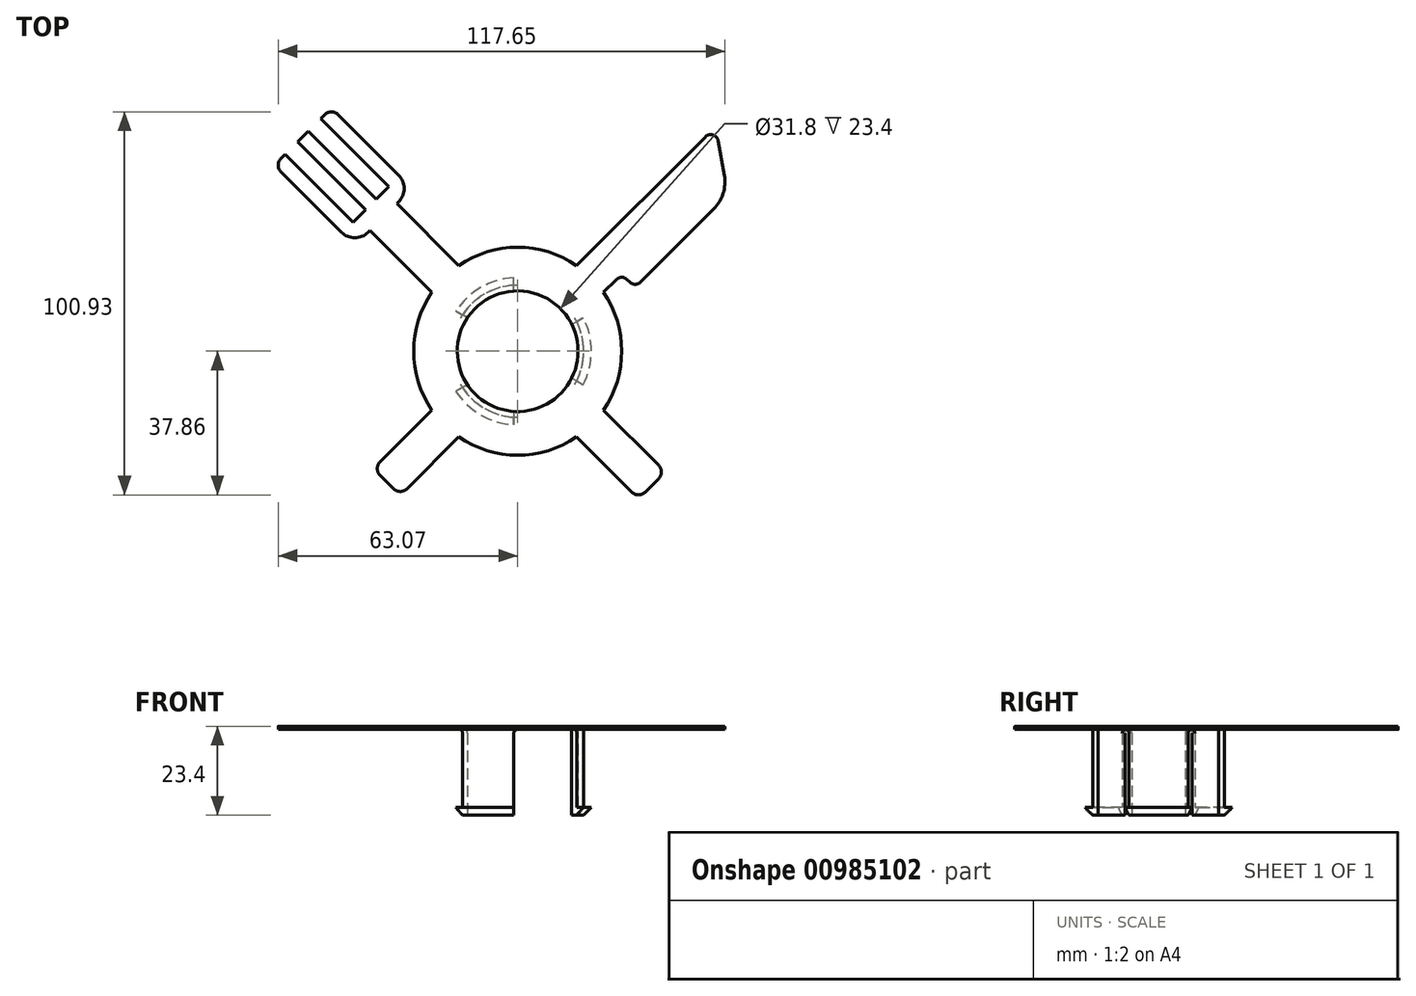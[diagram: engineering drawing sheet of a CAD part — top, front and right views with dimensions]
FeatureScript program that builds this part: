
annotation { "Feature Type Name" : "Feature", "Feature Type Description" : "" }
export const myFeature = defineFeature(function(context is Context, id is Id, definition is map)
    precondition{}
    {
        {
            var Q0;
            Q0=qCreatedBy(makeId("Top.planeOp"),FACE);
            var sketch = newSketch(context, id + "F0", { "sketchPlane" : qUnion([Q0])});
            skCircle(sketch, "E0", {"center": v(0, 0) * mm, "radius": 17.4 * mm});
            skCircle(sketch, "E1", {"center": v(0, 0) * mm, "radius": 15.9 * mm});
            skCircle(sketch, "E2", {"center": v(0, 0) * mm, "radius": 27.4 * mm});
            skLineSegment(sketch, "E3", {"start": v(0, 0) * mm, "end": v(0, 17.75) * mm, "construction": true});
            skText(sketch, "E4", { "text": "o", "fontName": "RobotoSlab-Bold.ttf"});
            skText(sketch, "E5", { "text": "u", "fontName": "RobotoSlab-Bold.ttf"});
            skText(sketch, "E6", { "text": "e", "fontName": "RobotoSlab-Bold.ttf"});
            skText(sketch, "E7", { "text": "i", "fontName": "RobotoSlab-Bold.ttf"});
            skText(sketch, "E8", { "text": "r", "fontName": "RobotoSlab-Bold.ttf"});
            skText(sketch, "E9", { "text": "c", "fontName": "RobotoSlab-Bold.ttf"});
            skText(sketch, "E10", { "text": "e", "fontName": "RobotoSlab-Bold.ttf"});
            skText(sketch, "E11", { "text": "o", "fontName": "RobotoSlab-Bold.ttf"});
            skText(sketch, "E12", { "text": "r", "fontName": "RobotoSlab-Bold.ttf"});
            skText(sketch, "E13", { "text": "n", "fontName": "RobotoSlab-Bold.ttf"});
            skLineSegment(sketch, "E14.2.0", {"start": v(0, 0) * mm, "end": v(-15.37, 8.88) * mm, "construction": true});
            skLineSegment(sketch, "E14.3.0", {"start": v(0, 0) * mm, "end": v(-17.75, 0) * mm, "construction": true});
            skLineSegment(sketch, "E14.4.0", {"start": v(0, 0) * mm, "end": v(-15.37, -8.88) * mm, "construction": true});
            skLineSegment(sketch, "E14.5.0", {"start": v(0, 0) * mm, "end": v(-8.88, -15.37) * mm, "construction": true});
            skLineSegment(sketch, "E14.6.0", {"start": v(0, 0) * mm, "end": v(0, -17.75) * mm, "construction": true});
            skLineSegment(sketch, "E14.7.0", {"start": v(0, 0) * mm, "end": v(8.87, -15.37) * mm, "construction": true});
            skLineSegment(sketch, "E14.8.0", {"start": v(0, 0) * mm, "end": v(15.37, -8.88) * mm, "construction": true});
            skLineSegment(sketch, "E14.9.0", {"start": v(0, 0) * mm, "end": v(17.75, 0) * mm, "construction": true});
            skLineSegment(sketch, "E14.10.0", {"start": v(0, 0) * mm, "end": v(15.37, 8.87) * mm, "construction": true});
            skLineSegment(sketch, "E14.11.0", {"start": v(0, 0) * mm, "end": v(8.88, 15.37) * mm, "construction": true});
            skText(sketch, "E15", { "text": "S", "fontName": "RobotoSlab-Bold.ttf"});
            skLineSegment(sketch, "E16", {"start": v(0, 0) * mm, "end": v(-8.88, 15.37) * mm, "construction": true});
            const initialGuessF0  = {"E4": [-0.00328, 0.01775, 1, 0, 0.008], "E5": [0.0057, 0.0172, 0.86603, -0.5, 0.008], "E6": [0.01692, -0.0062, -0.5, -0.86603, 0.008], "E7": [-0.0071, -0.0164, -0.86603, 0.5, 0.008], "E8": [-0.01407, -0.01114, -0.5, 0.86603, 0.008], "E9": [0.01775, 0.0031, 0, -1, 0.008], "E10": [0.01156, -0.01382, -0.86603, -0.5, 0.008], "E11": [-0.01775, -0.00328, 0, 1, 0.008], "E12": [0.01407, 0.01114, 0.5, -0.86603, 0.008], "E13": [-0.01726, 0.0056, 0.5, 0.86603, 0.008], "E15": [-0.01195, 0.0136, 0.86603, 0.5, 0.008]};
            skSetInitialGuess(sketch, initialGuessF0);
            skSolve(sketch);
        }
        {
            var Q0;
            Q0=makeQuery(id+"F0.imprint","IMPRINT",FACE,{"disambiguationData":[TD([[makeQuery(id+"F0.imprint","IMPRINT",EDGE,{"derivedFrom":sQuery(id+"F0.wireOp",EDGE,"E0")}),1.0]])]});
            var Q1;
            Q1=makeQuery(id+"F0.imprint","IMPRINT",FACE,{"disambiguationData":[TD([[makeQuery(id+"F0.imprint","IMPRINT",EDGE,{"derivedFrom":sQuery(id+"F0.wireOp",EDGE,"E4.sketch_text.stroke-0")}),-1.0]])]});
            var Q2;
            Q2=makeQuery(id+"F0.imprint","IMPRINT",FACE,{"disambiguationData":[TD([[makeQuery(id+"F0.imprint","IMPRINT",EDGE,{"derivedFrom":sQuery(id+"F0.wireOp",EDGE,"E7.sketch_text.stroke-0")}),-1.0]])]});
            var Q3;
            Q3=makeQuery(id+"F0.imprint","IMPRINT",FACE,{"disambiguationData":[TD([[makeQuery(id+"F0.imprint","IMPRINT",EDGE,{"derivedFrom":sQuery(id+"F0.wireOp",EDGE,"E11.sketch_text.stroke-10")}),1.0]])]});
            var Q4;
            Q4=makeQuery(id+"F0.imprint","IMPRINT",FACE,{"disambiguationData":[TD([[makeQuery(id+"F0.imprint","IMPRINT",EDGE,{"derivedFrom":sQuery(id+"F0.wireOp",EDGE,"E9.sketch_text.stroke-0")}),-1.0]])]});
            var Q5;
            Q5=makeQuery(id+"F0.imprint","IMPRINT",FACE,{"disambiguationData":[TD([[makeQuery(id+"F0.imprint","IMPRINT",EDGE,{"derivedFrom":sQuery(id+"F0.wireOp",EDGE,"E10.sketch_text.stroke-0")}),-1.0]])]});
            var Q6;
            Q6=makeQuery(id+"F0.imprint","IMPRINT",FACE,{"disambiguationData":[TD([[makeQuery(id+"F0.imprint","IMPRINT",EDGE,{"derivedFrom":sQuery(id+"F0.wireOp",EDGE,"E6.sketch_text.stroke-0")}),-1.0]])]});
            var Q7;
            Q7=makeQuery(id+"F0.imprint","IMPRINT",FACE,{"disambiguationData":[TD([[makeQuery(id+"F0.imprint","IMPRINT",EDGE,{"derivedFrom":sQuery(id+"F0.wireOp",EDGE,"E12.sketch_text.stroke-0")}),-1.0]])]});
            var Q8;
            Q8=makeQuery(id+"F0.imprint","IMPRINT",FACE,{"disambiguationData":[TD([[makeQuery(id+"F0.imprint","IMPRINT",EDGE,{"derivedFrom":sQuery(id+"F0.wireOp",EDGE,"E5.sketch_text.stroke-0")}),-1.0]])]});
            var Q9;
            Q9=makeQuery(id+"F0.imprint","IMPRINT",FACE,{"disambiguationData":[TD([[makeQuery(id+"F0.imprint","IMPRINT",EDGE,{"derivedFrom":sQuery(id+"F0.wireOp",EDGE,"E0")}),-1.0]])]});
            var Q10;
            Q10=makeQuery(id+"F0.imprint","IMPRINT",FACE,{"disambiguationData":[TD([[makeQuery(id+"F0.imprint","IMPRINT",EDGE,{"derivedFrom":sQuery(id+"F0.wireOp",EDGE,"E5.sketch_text.stroke-10")}),1.0]])]});
            var Q11;
            Q11=makeQuery(id+"F0.imprint","IMPRINT",FACE,{"disambiguationData":[TD([[makeQuery(id+"F0.imprint","IMPRINT",EDGE,{"derivedFrom":sQuery(id+"F0.wireOp",EDGE,"E13.sketch_text.stroke-0")}),-1.0]])]});
            var Q12;
            Q12=makeQuery(id+"F0.imprint","IMPRINT",FACE,{"disambiguationData":[TD([[makeQuery(id+"F0.imprint","IMPRINT",EDGE,{"derivedFrom":sQuery(id+"F0.wireOp",EDGE,"E8.sketch_text.stroke-0")}),-1.0]])]});
            var Q13;
            Q13=makeQuery(id+"F0.imprint","IMPRINT",FACE,{"disambiguationData":[TD([[makeQuery(id+"F0.imprint","IMPRINT",EDGE,{"derivedFrom":sQuery(id+"F0.wireOp",EDGE,"E11.sketch_text.stroke-0")}),-1.0]])]});
            var Q14;
            Q14=makeQuery(id+"F0.imprint","IMPRINT",FACE,{"disambiguationData":[TD([[makeQuery(id+"F0.imprint","IMPRINT",EDGE,{"derivedFrom":sQuery(id+"F0.wireOp",EDGE,"E7.sketch_text.stroke-10")}),-1.0]])]});
            var Q15;
            Q15=makeQuery(id+"F0.imprint","IMPRINT",FACE,{"disambiguationData":[TD([[makeQuery(id+"F0.imprint","IMPRINT",EDGE,{"derivedFrom":sQuery(id+"F0.wireOp",EDGE,"E10.sketch_text.stroke-17")}),1.0]])]});
            var Q16;
            Q16=makeQuery(id+"F0.imprint","IMPRINT",FACE,{"disambiguationData":[TD([[makeQuery(id+"F0.imprint","IMPRINT",EDGE,{"derivedFrom":sQuery(id+"F0.wireOp",EDGE,"E15.sketch_text.stroke-0")}),-1.0]])]});
            var Q17;
            Q17=makeQuery(id+"F0.imprint","IMPRINT",FACE,{"disambiguationData":[TD([[makeQuery(id+"F0.imprint","IMPRINT",EDGE,{"derivedFrom":sQuery(id+"F0.wireOp",EDGE,"E4.sketch_text.stroke-10")}),1.0]])]});
            var Q18;
            Q18=makeQuery(id+"F0.imprint","IMPRINT",FACE,{"disambiguationData":[TD([[makeQuery(id+"F0.imprint","IMPRINT",EDGE,{"derivedFrom":sQuery(id+"F0.wireOp",EDGE,"E6.sketch_text.stroke-17")}),1.0]])]});
            extrude(context, id + "F1", {"entities" : qUnion([Q0, Q1, Q2, Q3, Q4, Q5, Q6, Q7, Q8, Q9, Q10, Q11, Q12, Q13, Q14, Q15, Q16, Q17, Q18]), "depth" : 0.8 * mm, "offsetDistance" : 25 * mm});
        }
        {
            var Q0;
            Q0=makeQuery(id+"F0.imprint","IMPRINT",FACE,{"disambiguationData":[TD([[makeQuery(id+"F0.imprint","IMPRINT",EDGE,{"derivedFrom":sQuery(id+"F0.wireOp",EDGE,"E0")}),1.0]])]});
            extrude(context, id + "F2", {"entities" : qUnion([Q0]), "operationType" : NewBodyOperationType.ADD, "oppositeDirection" : true, "depth" : 22.6 * mm, "offsetDistance" : 25 * mm});
        }
        {
            var Q0;
            Q0=makeQuery(id+"F2.opExtrude","CAP_FACE",FACE,{"disambiguationData":[OSD([sQuery(id+"F0.wireOp",EDGE,"E0"),sQuery(id+"F0.wireOp",EDGE,"E1")])],"isStart":false});
            var sketch = newSketch(context, id + "F3", { "sketchPlane" : qUnion([Q0])});
            skLineSegment(sketch, "E17.bottom", {"start": v(1, 0) * mm, "end": v(-1, 0) * mm});
            skLineSegment(sketch, "E17.top", {"start": v(1, -20) * mm, "end": v(-1, -20) * mm});
            skLineSegment(sketch, "E17.left", {"start": v(1, 0) * mm, "end": v(1, -20) * mm});
            skLineSegment(sketch, "E17.right", {"start": v(-1, 0) * mm, "end": v(-1, -20) * mm});
            skLineSegment(sketch, "E18.1.0", {"start": v(0.5, 0.87) * mm, "end": v(-0.5, -0.87) * mm});
            skLineSegment(sketch, "E18.1.1", {"start": v(17.82, -9.13) * mm, "end": v(16.82, -10.87) * mm});
            skLineSegment(sketch, "E18.1.2", {"start": v(-0.5, -0.87) * mm, "end": v(16.82, -10.87) * mm});
            skLineSegment(sketch, "E18.1.3", {"start": v(0.5, 0.87) * mm, "end": v(17.82, -9.13) * mm});
            skLineSegment(sketch, "E18.2.0", {"start": v(-0.5, 0.87) * mm, "end": v(0.5, -0.87) * mm});
            skLineSegment(sketch, "E18.2.1", {"start": v(16.82, 10.87) * mm, "end": v(17.82, 9.13) * mm});
            skLineSegment(sketch, "E18.2.2", {"start": v(0.5, -0.87) * mm, "end": v(17.82, 9.13) * mm});
            skLineSegment(sketch, "E18.2.3", {"start": v(-0.5, 0.87) * mm, "end": v(16.82, 10.87) * mm});
            skLineSegment(sketch, "E18.3.0", {"start": v(-1, 0) * mm, "end": v(1, 0) * mm});
            skLineSegment(sketch, "E18.3.1", {"start": v(-1, 20) * mm, "end": v(1, 20) * mm});
            skLineSegment(sketch, "E18.3.2", {"start": v(1, 0) * mm, "end": v(1, 20) * mm});
            skLineSegment(sketch, "E18.3.3", {"start": v(-1, 0) * mm, "end": v(-1, 20) * mm});
            skLineSegment(sketch, "E18.4.0", {"start": v(-0.5, -0.87) * mm, "end": v(0.5, 0.87) * mm});
            skLineSegment(sketch, "E18.4.1", {"start": v(-17.82, 9.13) * mm, "end": v(-16.82, 10.87) * mm});
            skLineSegment(sketch, "E18.4.2", {"start": v(0.5, 0.87) * mm, "end": v(-16.82, 10.87) * mm});
            skLineSegment(sketch, "E18.4.3", {"start": v(-0.5, -0.87) * mm, "end": v(-17.82, 9.13) * mm});
            skLineSegment(sketch, "E18.5.0", {"start": v(0.5, -0.87) * mm, "end": v(-0.5, 0.87) * mm});
            skLineSegment(sketch, "E18.5.1", {"start": v(-16.82, -10.87) * mm, "end": v(-17.82, -9.13) * mm});
            skLineSegment(sketch, "E18.5.2", {"start": v(-0.5, 0.87) * mm, "end": v(-17.82, -9.13) * mm});
            skLineSegment(sketch, "E18.5.3", {"start": v(0.5, -0.87) * mm, "end": v(-16.82, -10.87) * mm});
            skPoint(sketch, "E18.center", {"position": v(0, 0) * mm});
            skCircle(sketch, "E19", {"center": v(0, 0) * mm, "radius": 19.4 * mm});
            skSolve(sketch);
        }
        {
            var Q0;
            {var subQ0=sQuery(id+"F3.wireOp",EDGE,"E18.1.2");var subQ1=makeQuery(id+"F2.opExtrude","CAP_EDGE",EDGE,{"disambiguationData":[OSD([sQuery(id+"F0.wireOp",EDGE,"E1")])],"isStart":false});var subQ2=makeQuery(id+"F3.imprint","INTERSECT",VERTEX,{"derivedFrom":[subQ1,subQ0]});Q0=makeQuery(id+"F3.imprint","IMPRINT",FACE,{"disambiguationData":[TD([[makeQuery(id+"F3.imprint","IMPRINT",EDGE,{"disambiguationData":[TD([[subQ2,-1.0]])],"derivedFrom":subQ0}),1.0]])]});}
            var Q1;
            {var subQ0=sQuery(id+"F3.wireOp",EDGE,"E17.left");var subQ1=makeQuery(id+"F2.opExtrude","CAP_EDGE",EDGE,{"disambiguationData":[OSD([sQuery(id+"F0.wireOp",EDGE,"E1")])],"isStart":false});var subQ2=makeQuery(id+"F3.imprint","INTERSECT",VERTEX,{"derivedFrom":[subQ1,subQ0]});Q1=makeQuery(id+"F3.imprint","IMPRINT",FACE,{"disambiguationData":[TD([[makeQuery(id+"F3.imprint","IMPRINT",EDGE,{"disambiguationData":[TD([[subQ2,-1.0]])],"derivedFrom":subQ0}),-1.0]])]});}
            var Q2;
            {var subQ0=sQuery(id+"F3.wireOp",EDGE,"E18.5.2");var subQ1=makeQuery(id+"F2.opExtrude","CAP_EDGE",EDGE,{"disambiguationData":[OSD([sQuery(id+"F0.wireOp",EDGE,"E1")])],"isStart":false});var subQ2=makeQuery(id+"F3.imprint","INTERSECT",VERTEX,{"derivedFrom":[subQ1,subQ0]});Q2=makeQuery(id+"F3.imprint","IMPRINT",FACE,{"disambiguationData":[TD([[makeQuery(id+"F3.imprint","IMPRINT",EDGE,{"disambiguationData":[TD([[subQ2,-1.0]])],"derivedFrom":subQ0}),1.0]])]});}
            var Q3;
            {var subQ0=sQuery(id+"F3.wireOp",EDGE,"E18.4.2");var subQ1=makeQuery(id+"F2.opExtrude","CAP_EDGE",EDGE,{"disambiguationData":[OSD([sQuery(id+"F0.wireOp",EDGE,"E1")])],"isStart":false});var subQ2=makeQuery(id+"F3.imprint","INTERSECT",VERTEX,{"derivedFrom":[subQ1,subQ0]});Q3=makeQuery(id+"F3.imprint","IMPRINT",FACE,{"disambiguationData":[TD([[makeQuery(id+"F3.imprint","IMPRINT",EDGE,{"disambiguationData":[TD([[subQ2,-1.0]])],"derivedFrom":subQ0}),1.0]])]});}
            var Q4;
            {var subQ0=sQuery(id+"F3.wireOp",EDGE,"E18.3.2");var subQ1=makeQuery(id+"F2.opExtrude","CAP_EDGE",EDGE,{"disambiguationData":[OSD([sQuery(id+"F0.wireOp",EDGE,"E1")])],"isStart":false});var subQ2=makeQuery(id+"F3.imprint","INTERSECT",VERTEX,{"derivedFrom":[subQ1,subQ0]});Q4=makeQuery(id+"F3.imprint","IMPRINT",FACE,{"disambiguationData":[TD([[makeQuery(id+"F3.imprint","IMPRINT",EDGE,{"disambiguationData":[TD([[subQ2,-1.0]])],"derivedFrom":subQ0}),1.0]])]});}
            var Q5;
            {var subQ0=sQuery(id+"F3.wireOp",EDGE,"E18.2.2");var subQ1=makeQuery(id+"F2.opExtrude","CAP_EDGE",EDGE,{"disambiguationData":[OSD([sQuery(id+"F0.wireOp",EDGE,"E1")])],"isStart":false});var subQ2=makeQuery(id+"F3.imprint","INTERSECT",VERTEX,{"derivedFrom":[subQ1,subQ0]});Q5=makeQuery(id+"F3.imprint","IMPRINT",FACE,{"disambiguationData":[TD([[makeQuery(id+"F3.imprint","IMPRINT",EDGE,{"disambiguationData":[TD([[subQ2,-1.0]])],"derivedFrom":subQ0}),1.0]])]});}
            var Q6;
            {var subQ0=sQuery(id+"F3.wireOp",EDGE,"E17.left");var subQ1=makeQuery(id+"F2.opExtrude","CAP_EDGE",EDGE,{"disambiguationData":[OSD([sQuery(id+"F0.wireOp",EDGE,"E1")])],"isStart":false});var subQ2=makeQuery(id+"F3.imprint","INTERSECT",VERTEX,{"derivedFrom":[subQ1,subQ0]});Q6=makeQuery(id+"F3.imprint","IMPRINT",FACE,{"disambiguationData":[TD([[makeQuery(id+"F3.imprint","IMPRINT",EDGE,{"disambiguationData":[TD([[subQ2,-1.0]])],"derivedFrom":subQ0}),1.0]])]});}
            var Q7;
            {var subQ0=sQuery(id+"F3.wireOp",EDGE,"E18.4.3");var subQ1=makeQuery(id+"F2.opExtrude","CAP_EDGE",EDGE,{"disambiguationData":[OSD([sQuery(id+"F0.wireOp",EDGE,"E1")])],"isStart":false});var subQ2=makeQuery(id+"F3.imprint","INTERSECT",VERTEX,{"derivedFrom":[subQ1,subQ0]});Q7=makeQuery(id+"F3.imprint","IMPRINT",FACE,{"disambiguationData":[TD([[makeQuery(id+"F3.imprint","IMPRINT",EDGE,{"disambiguationData":[TD([[subQ2,-1.0]])],"derivedFrom":subQ0}),1.0]])]});}
            var Q8;
            {var subQ0=sQuery(id+"F3.wireOp",EDGE,"E18.2.3");var subQ1=makeQuery(id+"F2.opExtrude","CAP_EDGE",EDGE,{"disambiguationData":[OSD([sQuery(id+"F0.wireOp",EDGE,"E1")])],"isStart":false});var subQ2=makeQuery(id+"F3.imprint","INTERSECT",VERTEX,{"derivedFrom":[subQ1,subQ0]});Q8=makeQuery(id+"F3.imprint","IMPRINT",FACE,{"disambiguationData":[TD([[makeQuery(id+"F3.imprint","IMPRINT",EDGE,{"disambiguationData":[TD([[subQ2,-1.0]])],"derivedFrom":subQ0}),1.0]])]});}
            var Q9;
            Q9=makeQuery(id+"F1.opExtrude","CAP_FACE",FACE,{"disambiguationData":[OSD([sQuery(id+"F0.wireOp",EDGE,"E1"),sQuery(id+"F0.wireOp",EDGE,"E2")])],"isStart":true});
            extrude(context, id + "F4", {"entities" : qUnion([Q0, Q1, Q2, Q3, Q4, Q5, Q6, Q7, Q8]), "operationType" : NewBodyOperationType.REMOVE, "endBound" : BoundingType.UP_TO_SURFACE, "oppositeDirection" : true, "depth" : 25 * mm, "endBoundEntityFace" : qUnion([Q9]), "offsetDistance" : 25 * mm});
        }
        {
            var Q0;
            {var subQ0=sQuery(id+"F3.wireOp",EDGE,"E19");var subQ1=sQuery(id+"F3.wireOp",EDGE,"E18.1.3");var subQ2=makeQuery(id+"F3.imprint","INTERSECT",VERTEX,{"derivedFrom":[subQ1,subQ0]});Q0=makeQuery(id+"F3.imprint","IMPRINT",FACE,{"disambiguationData":[TD([[makeQuery(id+"F3.imprint","IMPRINT",EDGE,{"disambiguationData":[TD([[subQ2,1.0]])],"derivedFrom":subQ1}),1.0]])]});}
            var Q1;
            {var subQ0=sQuery(id+"F3.wireOp",EDGE,"E19");var subQ1=sQuery(id+"F3.wireOp",EDGE,"E17.right");var subQ2=makeQuery(id+"F3.imprint","INTERSECT",VERTEX,{"derivedFrom":[subQ1,subQ0]});Q1=makeQuery(id+"F3.imprint","IMPRINT",FACE,{"disambiguationData":[TD([[makeQuery(id+"F3.imprint","IMPRINT",EDGE,{"disambiguationData":[TD([[subQ2,1.0]])],"derivedFrom":subQ1}),-1.0]])]});}
            var Q2;
            {var subQ0=sQuery(id+"F3.wireOp",EDGE,"E19");var subQ1=sQuery(id+"F3.wireOp",EDGE,"E18.3.3");var subQ2=makeQuery(id+"F3.imprint","INTERSECT",VERTEX,{"derivedFrom":[subQ1,subQ0]});Q2=makeQuery(id+"F3.imprint","IMPRINT",FACE,{"disambiguationData":[TD([[makeQuery(id+"F3.imprint","IMPRINT",EDGE,{"disambiguationData":[TD([[subQ2,1.0]])],"derivedFrom":subQ1}),1.0]])]});}
            extrude(context, id + "F5", {"entities" : qUnion([Q0, Q1, Q2]), "operationType" : NewBodyOperationType.ADD, "oppositeDirection" : true, "depth" : 2 * mm, "offsetDistance" : 25 * mm});
        }
        {
            var Q0;
            {var subQ0=sQuery(id+"F3.wireOp",EDGE,"E19");Q0=makeQuery(id+"F5.opExtrude","CAP_EDGE",EDGE,{"disambiguationData":[OSD([subQ0]),TDD([makeQuery(id+"F3.imprint","IMPRINT",EDGE,{"disambiguationData":[TD([[makeQuery(id+"F3.imprint","INTERSECT",VERTEX,{"derivedFrom":[sQuery(id+"F3.wireOp",EDGE,"E18.1.3"),subQ0]}),-1.0]])],"derivedFrom":subQ0})])],"isStart":true});}
            var Q1;
            {var subQ0=sQuery(id+"F3.wireOp",EDGE,"E19");Q1=makeQuery(id+"F5.opExtrude","CAP_EDGE",EDGE,{"disambiguationData":[OSD([subQ0]),TDD([makeQuery(id+"F3.imprint","IMPRINT",EDGE,{"disambiguationData":[TD([[makeQuery(id+"F3.imprint","INTERSECT",VERTEX,{"derivedFrom":[sQuery(id+"F3.wireOp",EDGE,"E18.2.3"),subQ0]}),-1.0]])],"derivedFrom":subQ0})])],"isStart":true});}
            var Q2;
            {var subQ0=sQuery(id+"F3.wireOp",EDGE,"E19");Q2=makeQuery(id+"F5.opExtrude","CAP_EDGE",EDGE,{"disambiguationData":[OSD([subQ0]),TDD([makeQuery(id+"F3.imprint","IMPRINT",EDGE,{"disambiguationData":[TD([[makeQuery(id+"F3.imprint","INTERSECT",VERTEX,{"derivedFrom":[sQuery(id+"F3.wireOp",EDGE,"E18.3.3"),subQ0]}),-1.0]])],"derivedFrom":subQ0})])],"isStart":true});}
            var Q3;
            {var subQ0=sQuery(id+"F3.wireOp",EDGE,"E19");Q3=makeQuery(id+"F5.opExtrude","CAP_EDGE",EDGE,{"disambiguationData":[OSD([subQ0]),TDD([makeQuery(id+"F3.imprint","IMPRINT",EDGE,{"disambiguationData":[TD([[makeQuery(id+"F3.imprint","INTERSECT",VERTEX,{"derivedFrom":[sQuery(id+"F3.wireOp",EDGE,"E17.right"),subQ0]}),1.0]])],"derivedFrom":subQ0})])],"isStart":true});}
            var Q4;
            {var subQ0=sQuery(id+"F3.wireOp",EDGE,"E19");Q4=makeQuery(id+"F5.opExtrude","CAP_EDGE",EDGE,{"disambiguationData":[OSD([subQ0]),TDD([makeQuery(id+"F3.imprint","IMPRINT",EDGE,{"disambiguationData":[TD([[makeQuery(id+"F3.imprint","INTERSECT",VERTEX,{"derivedFrom":[sQuery(id+"F3.wireOp",EDGE,"E17.left"),subQ0]}),-1.0]])],"derivedFrom":subQ0})])],"isStart":true});}
            var Q5;
            {var subQ0=sQuery(id+"F3.wireOp",EDGE,"E19");Q5=makeQuery(id+"F5.opExtrude","CAP_EDGE",EDGE,{"disambiguationData":[OSD([subQ0]),TDD([makeQuery(id+"F3.imprint","IMPRINT",EDGE,{"disambiguationData":[TD([[makeQuery(id+"F3.imprint","INTERSECT",VERTEX,{"derivedFrom":[sQuery(id+"F3.wireOp",EDGE,"E18.4.3"),subQ0]}),-1.0]])],"derivedFrom":subQ0})])],"isStart":true});}
            chamfer(context, id + "F6", {"entities" : qUnion([Q0, Q1, Q2, Q3, Q4, Q5]), "width" : 2 * mm, "tangentPropagation" : true});
        }
        {
            var Q0;
            {var subQ0=sQuery(id+"F3.wireOp",EDGE,"E17.right");var subQ2=sQuery(id+"F0.wireOp",EDGE,"E0");Q0=makeQuery(id+"F4.boolean.opBoolean","SPLIT",EDGE,{"disambiguationData":[TD([makeQuery(id+"F4.opExtrude","SWEPT_FACE",FACE,{"disambiguationData":[OSD([subQ0])]})])],"derivedFrom":makeQuery(id+"F2.opExtrude","CAP_EDGE",EDGE,{"disambiguationData":[OSD([subQ2])],"isStart":true})});}
            var Q1;
            {var subQ1=sQuery(id+"F0.wireOp",EDGE,"E0");var subQ2=sQuery(id+"F3.wireOp",EDGE,"E18.3.3");Q1=makeQuery(id+"F4.boolean.opBoolean","SPLIT",EDGE,{"disambiguationData":[TD([makeQuery(id+"F4.opExtrude","SWEPT_FACE",FACE,{"disambiguationData":[OSD([subQ2])]})])],"derivedFrom":makeQuery(id+"F2.opExtrude","CAP_EDGE",EDGE,{"disambiguationData":[OSD([subQ1])],"isStart":true})});}
            var Q2;
            {var subQ0=sQuery(id+"F3.wireOp",EDGE,"E18.1.3");var subQ2=sQuery(id+"F0.wireOp",EDGE,"E0");Q2=makeQuery(id+"F4.boolean.opBoolean","SPLIT",EDGE,{"disambiguationData":[TD([makeQuery(id+"F4.opExtrude","SWEPT_FACE",FACE,{"disambiguationData":[OSD([subQ0])]})])],"derivedFrom":makeQuery(id+"F2.opExtrude","CAP_EDGE",EDGE,{"disambiguationData":[OSD([subQ2])],"isStart":true})});}
            var Q3;
            Q3=makeQuery(id+"F4.boolean.opBoolean","COPY",EDGE,{"derivedFrom":makeQuery(id+"F4.opExtrude","CAP_EDGE",EDGE,{"disambiguationData":[OSD([sQuery(id+"F3.wireOp",EDGE,"E18.2.2")])],"isStart":false})});
            var Q4;
            Q4=makeQuery(id+"F4.boolean.opBoolean","COPY",EDGE,{"derivedFrom":makeQuery(id+"F4.opExtrude","CAP_EDGE",EDGE,{"disambiguationData":[OSD([sQuery(id+"F3.wireOp",EDGE,"E18.3.3")])],"isStart":false})});
            var Q5;
            Q5=makeQuery(id+"F4.boolean.opBoolean","COPY",EDGE,{"derivedFrom":makeQuery(id+"F4.opExtrude","CAP_EDGE",EDGE,{"disambiguationData":[OSD([sQuery(id+"F3.wireOp",EDGE,"E18.1.3")])],"isStart":false})});
            var Q6;
            Q6=makeQuery(id+"F4.boolean.opBoolean","COPY",EDGE,{"derivedFrom":makeQuery(id+"F4.opExtrude","CAP_EDGE",EDGE,{"disambiguationData":[OSD([sQuery(id+"F3.wireOp",EDGE,"E17.right")])],"isStart":false})});
            var Q7;
            Q7=makeQuery(id+"F4.boolean.opBoolean","COPY",EDGE,{"derivedFrom":makeQuery(id+"F4.opExtrude","CAP_EDGE",EDGE,{"disambiguationData":[OSD([sQuery(id+"F3.wireOp",EDGE,"E18.5.3")])],"isStart":false})});
            var Q8;
            Q8=makeQuery(id+"F4.boolean.opBoolean","COPY",EDGE,{"derivedFrom":makeQuery(id+"F4.opExtrude","CAP_EDGE",EDGE,{"disambiguationData":[OSD([sQuery(id+"F3.wireOp",EDGE,"E18.4.2")])],"isStart":false})});
            fillet(context, id + "F7", {"entities" : qUnion([Q0, Q1, Q2, Q3, Q4, Q5, Q6, Q7, Q8]), "radius" : 1 * mm, "tangentPropagation" : true, "allowEdgeOverflow" : false});
        }
        {
            var Q0;
            Q0=makeQuery(id+"F1.opExtrude","CAP_FACE",FACE,{"disambiguationData":[OSD([sQuery(id+"F0.wireOp",EDGE,"E1"),sQuery(id+"F0.wireOp",EDGE,"E2")])],"isStart":false});
            var sketch = newSketch(context, id + "F8", { "sketchPlane" : qUnion([Q0])});
            skLineSegment(sketch, "E20.bottom", {"start": v(-38.9, 31.82) * mm, "end": v(30.05, -37.12) * mm});
            skLineSegment(sketch, "E20.top", {"start": v(-31.82, 38.9) * mm, "end": v(37.12, -30.05) * mm});
            skLineSegment(sketch, "E20.left", {"start": v(-38.9, 31.82) * mm, "end": v(-31.82, 38.9) * mm});
            skLineSegment(sketch, "E20.right", {"start": v(33.59, -37.12) * mm, "end": v(37.12, -33.59) * mm});
            skPoint(sketch, "E20.middle", {"position": v(0, 0) * mm});
            skLineSegment(sketch, "E21", {"start": v(35.36, -35.36) * mm, "end": v(0, 0) * mm, "construction": true});
            skLineSegment(sketch, "E22", {"start": v(0, 0) * mm, "end": v(0, -3.91) * mm});
            skLineSegment(sketch, "E23", {"start": v(-35.36, 35.36) * mm, "end": v(-56.57, 56.57) * mm});
            skLineSegment(sketch, "E24", {"start": v(-56.57, 56.57) * mm, "end": v(-55.15, 57.98) * mm});
            skLineSegment(sketch, "E25", {"start": v(-55.15, 57.98) * mm, "end": v(-37.23, 40.06) * mm});
            skLineSegment(sketch, "E26", {"start": v(-37.23, 40.06) * mm, "end": v(-33.94, 43.35) * mm});
            skLineSegment(sketch, "E27", {"start": v(-33.94, 43.35) * mm, "end": v(-51.86, 61.28) * mm});
            skLineSegment(sketch, "E28", {"start": v(-51.86, 61.28) * mm, "end": v(-50.8, 62.34) * mm});
            skLineSegment(sketch, "E29", {"start": v(-47.26, 62.34) * mm, "end": v(-31.35, 46.43) * mm});
            skLineSegment(sketch, "E30", {"start": v(-31.35, 39.36) * mm, "end": v(-31.82, 38.9) * mm});
            skLineSegment(sketch, "E31.MirrorCS", {"start": v(-62.34, 47.26) * mm, "end": v(-46.43, 31.35) * mm});
            skLineSegment(sketch, "E32.MirrorCS", {"start": v(-56.57, 56.57) * mm, "end": v(-57.98, 55.15) * mm});
            skLineSegment(sketch, "E33.MirrorCS", {"start": v(-39.36, 31.35) * mm, "end": v(-38.9, 31.82) * mm});
            skLineSegment(sketch, "E34.MirrorCS", {"start": v(-57.98, 55.15) * mm, "end": v(-40.06, 37.23) * mm});
            skLineSegment(sketch, "E35.MirrorCS", {"start": v(-61.28, 51.86) * mm, "end": v(-62.34, 50.8) * mm});
            skLineSegment(sketch, "E36.MirrorCS", {"start": v(-43.35, 33.94) * mm, "end": v(-61.28, 51.86) * mm});
            skLineSegment(sketch, "E37.MirrorCS", {"start": v(-40.06, 37.23) * mm, "end": v(-43.35, 33.94) * mm});
            skPoint(sketch, "E38.visualSharp", {"position": v(-42.9, 27.82) * mm});
            skArc(sketch, "E38.filletArc", {"start": v(-46.43, 31.35) * mm, "mid": v(-42.9, 29.89) * mm, "end": v(-39.36, 31.35) * mm});
            skPoint(sketch, "E39.visualSharp", {"position": v(-27.82, 42.9) * mm});
            skArc(sketch, "E39.filletArc", {"start": v(-31.35, 39.36) * mm, "mid": v(-29.89, 42.9) * mm, "end": v(-31.35, 46.43) * mm});
            skPoint(sketch, "E40.visualSharp", {"position": v(31.82, -38.9) * mm});
            skArc(sketch, "E40.filletArc", {"start": v(30.05, -37.12) * mm, "mid": v(31.82, -37.86) * mm, "end": v(33.59, -37.12) * mm});
            skPoint(sketch, "E41.visualSharp", {"position": v(38.9, -31.82) * mm});
            skArc(sketch, "E41.filletArc", {"start": v(37.12, -33.59) * mm, "mid": v(37.86, -31.82) * mm, "end": v(37.12, -30.05) * mm});
            skPoint(sketch, "E42.visualSharp", {"position": v(-64.1, 49.03) * mm});
            skArc(sketch, "E42.filletArc", {"start": v(-62.34, 50.8) * mm, "mid": v(-63.07, 49.03) * mm, "end": v(-62.34, 47.26) * mm});
            skPoint(sketch, "E43.visualSharp", {"position": v(-49.03, 64.1) * mm});
            skArc(sketch, "E43.filletArc", {"start": v(-47.26, 62.34) * mm, "mid": v(-49.03, 63.07) * mm, "end": v(-50.8, 62.34) * mm});
            skLineSegment(sketch, "E44.bottom", {"start": v(-29.17, -36.24) * mm, "end": v(25.99, 18.92) * mm});
            skLineSegment(sketch, "E44.top", {"start": v(-36.24, -29.17) * mm, "end": v(30.94, 38) * mm});
            skLineSegment(sketch, "E44.left", {"start": v(-32.7, -36.24) * mm, "end": v(-36.24, -32.7) * mm});
            skLineSegment(sketch, "E44.right", {"start": v(38, 30.94) * mm, "end": v(30.94, 38) * mm});
            skLineSegment(sketch, "E45", {"start": v(-34.47, -34.47) * mm, "end": v(0, 0) * mm, "construction": true});
            skLineSegment(sketch, "E46", {"start": v(30.94, 38) * mm, "end": v(49.43, 56.5) * mm});
            skLineSegment(sketch, "E47", {"start": v(52.82, 55.44) * mm, "end": v(54.43, 46.33) * mm});
            skLineSegment(sketch, "E48", {"start": v(51.65, 37.51) * mm, "end": v(41.54, 27.4) * mm});
            skLineSegment(sketch, "E49", {"start": v(41.54, 27.4) * mm, "end": v(38, 30.94) * mm});
            skLineSegment(sketch, "E50", {"start": v(41.54, 27.4) * mm, "end": v(32.35, 18.2) * mm});
            skLineSegment(sketch, "E51", {"start": v(29.52, 18.2) * mm, "end": v(28.81, 18.92) * mm});
            skPoint(sketch, "E52.visualSharp", {"position": v(55.34, 41.2) * mm});
            skArc(sketch, "E52.filletArc", {"start": v(51.65, 37.51) * mm, "mid": v(54.12, 41.58) * mm, "end": v(54.43, 46.33) * mm});
            skPoint(sketch, "E53.visualSharp", {"position": v(52.15, 59.22) * mm});
            skArc(sketch, "E53.filletArc", {"start": v(52.82, 55.44) * mm, "mid": v(51.45, 57) * mm, "end": v(49.43, 56.5) * mm});
            skPoint(sketch, "E54.visualSharp", {"position": v(30.94, 16.8) * mm});
            skArc(sketch, "E54.filletArc", {"start": v(29.52, 18.2) * mm, "mid": v(30.94, 17.62) * mm, "end": v(32.35, 18.2) * mm});
            skPoint(sketch, "E55.newPointB", {"position": v(38, 30.94) * mm});
            skArc(sketch, "E55.filletArc", {"start": v(28.81, 18.92) * mm, "mid": v(27.4, 19.5) * mm, "end": v(25.99, 18.92) * mm});
            skPoint(sketch, "E56.visualSharp", {"position": v(-38, -30.94) * mm});
            skArc(sketch, "E56.filletArc", {"start": v(-36.24, -29.17) * mm, "mid": v(-36.97, -30.94) * mm, "end": v(-36.24, -32.7) * mm});
            skPoint(sketch, "E57.visualSharp", {"position": v(-30.94, -38) * mm});
            skArc(sketch, "E57.filletArc", {"start": v(-32.7, -36.24) * mm, "mid": v(-30.94, -36.97) * mm, "end": v(-29.17, -36.24) * mm});
            skSolve(sketch);
        }
        {
            var Q0;
            {var subQ1=sQuery(id+"F8.wireOp",EDGE,"E20.bottom");var subQ6=makeQuery(id+"F1.opExtrude","CAP_EDGE",EDGE,{"disambiguationData":[OSD([sQuery(id+"F0.wireOp",EDGE,"E2")])],"isStart":false});var subQ8=makeQuery(id+"F8.imprint","INTERSECT",VERTEX,{"disambiguationData":[OD(0.0)],"derivedFrom":[subQ6,subQ1]});Q0=makeQuery(id+"F8.imprint","IMPRINT",FACE,{"disambiguationData":[TD([[makeQuery(id+"F8.imprint","IMPRINT",EDGE,{"disambiguationData":[TD([[subQ8,1.0]])],"derivedFrom":subQ6}),-1.0]])]});}
            var Q1;
            {var subQ2=sQuery(id+"F8.wireOp",EDGE,"E23");Q1=makeQuery(id+"F8.imprint","IMPRINT",FACE,{"disambiguationData":[TD([[makeQuery(id+"F8.imprint","IMPRINT",EDGE,{"derivedFrom":subQ2}),-1.0]])]});}
            var Q2;
            {var subQ1=sQuery(id+"F8.wireOp",EDGE,"E23");Q2=makeQuery(id+"F8.imprint","IMPRINT",FACE,{"disambiguationData":[TD([[makeQuery(id+"F8.imprint","IMPRINT",EDGE,{"derivedFrom":subQ1}),1.0]])]});}
            var Q3;
            Q3=makeQuery(id+"F8.imprint","IMPRINT",FACE,{"disambiguationData":[TD([[makeQuery(id+"F8.imprint","IMPRINT",EDGE,{"derivedFrom":sQuery(id+"F8.wireOp",EDGE,"E44.right")}),-1.0]])]});
            var Q4;
            {var subQ0=sQuery(id+"F8.wireOp",EDGE,"E44.right");Q4=makeQuery(id+"F8.imprint","IMPRINT",FACE,{"disambiguationData":[TD([[makeQuery(id+"F8.imprint","IMPRINT",EDGE,{"derivedFrom":subQ0}),1.0]])]});}
            var Q5;
            Q5=makeQuery(id+"F8.imprint","IMPRINT",FACE,{"disambiguationData":[TD([[makeQuery(id+"F8.imprint","IMPRINT",EDGE,{"derivedFrom":sQuery(id+"F8.wireOp",EDGE,"E20.right")}),1.0]])]});
            var Q6;
            Q6=makeQuery(id+"F8.imprint","IMPRINT",FACE,{"disambiguationData":[TD([[makeQuery(id+"F8.imprint","IMPRINT",EDGE,{"derivedFrom":sQuery(id+"F8.wireOp",EDGE,"E44.left")}),-1.0]])]});
            var Q7;
            {var subQ0=sQuery(id+"F0.wireOp",EDGE,"E1");var subQ1=sQuery(id+"F0.wireOp",EDGE,"E0");Q7=makeQuery(id+"F4.boolean.opBoolean","MERGE",FACE,{"derivedFrom":[makeQuery(id+"F1.opExtrude","CAP_FACE",FACE,{"disambiguationData":[OSD([subQ0,sQuery(id+"F0.wireOp",EDGE,"E2")])],"isStart":true})],"fromTools":[makeQuery(id+"F4.opExtrude","CAP_FACE",FACE,{"disambiguationData":[OSD([subQ1,subQ0,sQuery(id+"F3.wireOp",EDGE,"E17.right"),sQuery(id+"F3.wireOp",EDGE,"E18.1.3")])],"isStart":false}),makeQuery(id+"F4.opExtrude","CAP_FACE",FACE,{"disambiguationData":[OSD([subQ1,subQ0,sQuery(id+"F3.wireOp",EDGE,"E18.2.2"),sQuery(id+"F3.wireOp",EDGE,"E18.3.3")])],"isStart":false}),makeQuery(id+"F4.opExtrude","CAP_FACE",FACE,{"disambiguationData":[OSD([subQ1,subQ0,sQuery(id+"F3.wireOp",EDGE,"E18.4.2"),sQuery(id+"F3.wireOp",EDGE,"E18.5.3")])],"isStart":false})]});}
            extrude(context, id + "F9", {"entities" : qUnion([Q0, Q1, Q2, Q3, Q4, Q5, Q6]), "operationType" : NewBodyOperationType.ADD, "endBound" : BoundingType.UP_TO_SURFACE, "oppositeDirection" : true, "depth" : 25 * mm, "endBoundEntityFace" : qUnion([Q7]), "offsetDistance" : 25 * mm});
        }
    });
